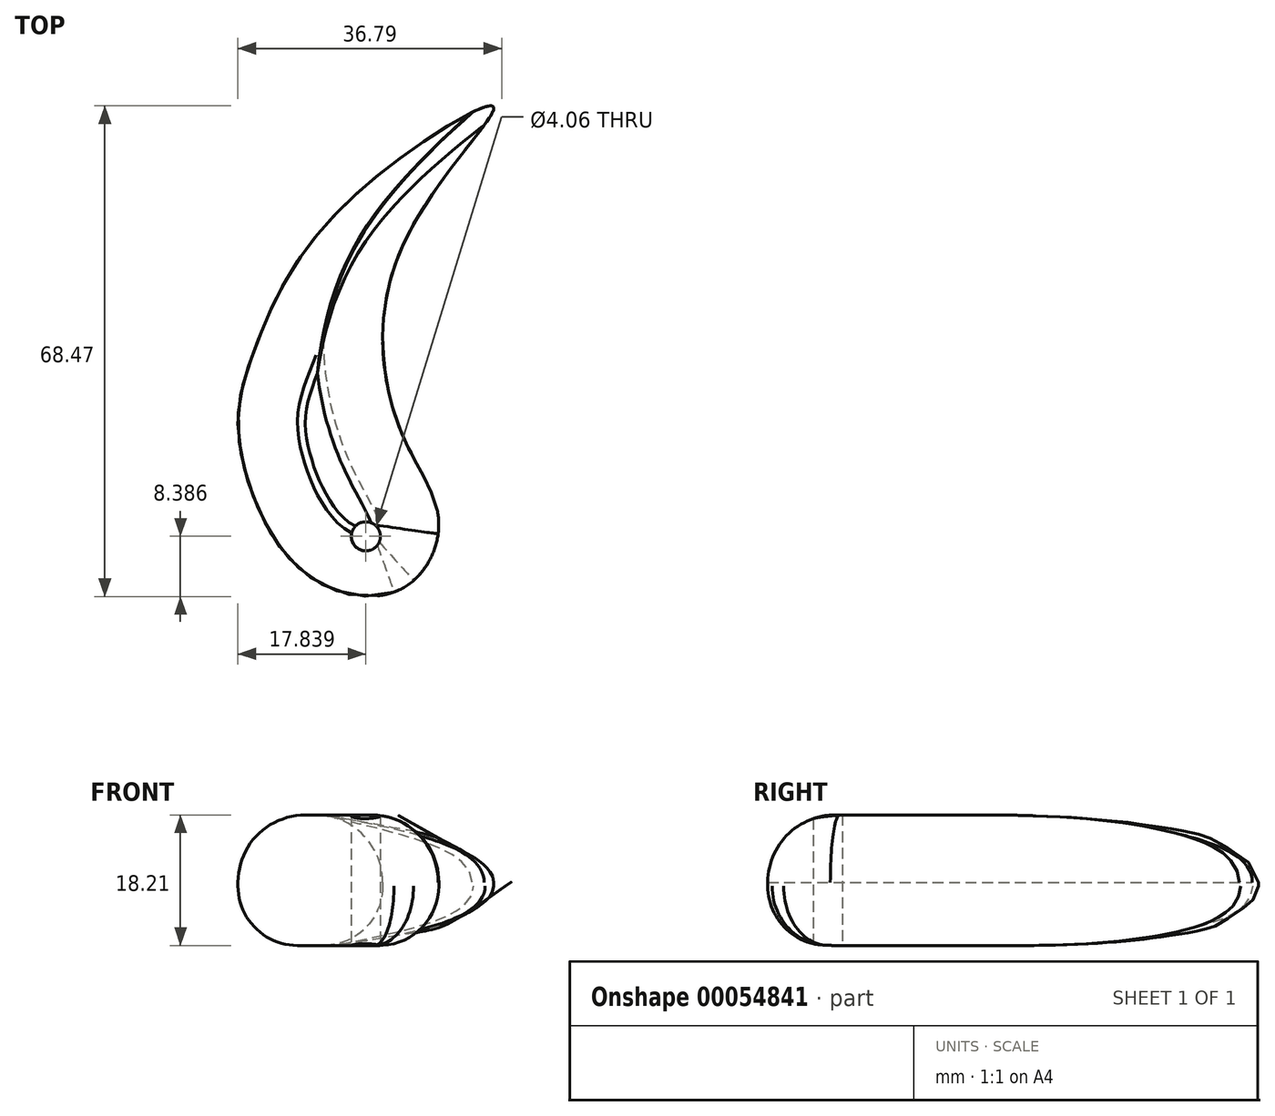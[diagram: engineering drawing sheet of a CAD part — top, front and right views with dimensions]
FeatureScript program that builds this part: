
annotation { "Feature Type Name" : "Feature", "Feature Type Description" : "" }
export const myFeature = defineFeature(function(context is Context, id is Id, definition is map)
    precondition{}
    {
        {
            var Q0;
            Q0=qCreatedBy(makeId("Top.planeOp"),FACE);
            var sketch = newSketch(context, id + "F0", { "sketchPlane" : qUnion([Q0])});
            skFitSpline(sketch, "E0", {"points": [v(0, -21.26) * mm, v(-13.85, -19.04) * mm, v(-22.91, 0) * mm, v(-20.72, 11.97) * mm, v(-8.35, 32) * mm, v(12.6, 45.93) * mm, v(0, 26.6) * mm, v(0, 0) * mm, v(5, -11.84) * mm, v(0, -21.26) * mm]});
            skSolve(sketch);
        }
        {
            var Q0;
            Q0=makeQuery(id+"F0.imprint","IMPRINT",FACE,{"disambiguationData":[TD([[makeQuery(id+"F0.imprint","IMPRINT",EDGE,{"derivedFrom":sQuery(id+"F0.wireOp",EDGE,"E0")}),-1.0]])]});
            extrude(context, id + "F1", {"entities" : qUnion([Q0]), "depth" : 18.21 * mm});
        }
        {
            var Q0;
            Q0=makeQuery(id+"F1.opExtrude","CAP_EDGE",EDGE,{"disambiguationData":[OSD([sQuery(id+"F0.wireOp",EDGE,"E0")])],"isStart":true});
            fillet(context, id + "F2", {"entities" : qUnion([Q0]), "radius" : 8.29 * mm, "tangentPropagation" : true, "allowEdgeOverflow" : false});
        }
        {
            var Q0;
            Q0=makeQuery(id+"F1.opExtrude","CAP_EDGE",EDGE,{"disambiguationData":[OSD([sQuery(id+"F0.wireOp",EDGE,"E0")])],"isStart":false});
            fillet(context, id + "F3", {"entities" : qUnion([Q0]), "radius" : 9.38 * mm, "tangentPropagation" : true, "allowEdgeOverflow" : false});
        }
        {
            var Q0;
            Q0=qCreatedBy(makeId("Top.planeOp"),FACE);
            var sketch = newSketch(context, id + "F4", { "sketchPlane" : qUnion([Q0])});
            skCircle(sketch, "E1", {"center": v(-5.16, -14.04) * mm, "radius": 2.3 * mm});
            skSolve(sketch);
        }
        {
            var Q0;
            Q0=sQuery(id+"F4.wireOp",VERTEX,"E1.center");
            var Q1;
            Q1=makeQuery(id+"F1.opExtrude","SWEPT_BODY",BODY,{"disambiguationData":[OSD([sQuery(id+"F0.wireOp",EDGE,"E0")])]});
            hole(context, id + "F5", {"style" : HoleStyle.SIMPLE, "holeDiameter" : 4.06 * mm, "endStyle" : HoleEndStyle.THROUGH, "oppositeDirection" : true, "locations" : qUnion([Q0]), "scope" : qUnion([Q1])});
        }
    });
